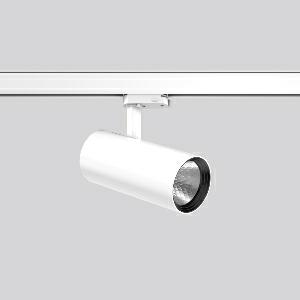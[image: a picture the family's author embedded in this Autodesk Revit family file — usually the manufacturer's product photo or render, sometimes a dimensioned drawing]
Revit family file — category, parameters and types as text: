
# Revit family: deecos_s_mini_742205_002_2_76_f33d
name_source: partatom
category: Lighting Fixtures
units: mm (PartAtom-declared; Revit-internal decimal feet)

## family parameters
Cut with Voids When Loaded = No
Host = Face
Light Source = No
Part Type = Normal
Room Calculation Point = No
Round Connector Dimension = Use Diameter
Shared = No

## types (1)
- DEECOS S mini (1 x LED Modul 927, 3500 lm, 2700)
    Apparent Load = 29 VA
    Approval mark = CE
    CIE Flux Codes = 95 99 100 100 100
    Color Rendering = 92
    Color Temperature = 2700
    Default Elevation = 1800 mm
    Description = Series: DEECOS S mini
LED surface-mounted projector in modern design with no visible cooling ribs. Housing: die-cast aluminium, powder-coated. Rotation range: 356°. Swivel range: 90°. Black plastic ring and recessed LED to prevent glare from the side. Optical assembly with reflector made of MIRO-Silver with 98% total light reflection for outstanding efficiency - can be changed without tools. Best colour rendering index Ra>90. With adapter for RZB 3-circuit DALI tracks. Suitable for Track on ceiling, Wall track. High quality converter without flickering and stroboscopic effect. The following accessories can be mounted without use of tools: interchangeable lenses, decorative glasses, honeycomb louvre, clear and frosted diffusers, white interchangeable plastic ring. 
Colour: traffic white, matt (RAL 9016)
Diameter: 87 mm
Height: 214 mm
Lamp: LED
Socket: without socket
Colour temperature: 2700K
Colour rendering index (CRI): 92
System power: 29 W
Rated luminous flux: 3500 lm
Luminous efficiency: 121 lm/W
Control gear: Converter, dimmable, DALI
Protection class: I
Type of protection: IP 20
    Height = 214 mm
    Lamp = 1 x LED Modul 927
    Lamp Light Flux = 3500 lm
    Lamp count = 1
    Length = 87 mm
    Lifetime = 50000 h
    Luminous efficacy = 121 lm/W
    Manufacturer = RZB
    ModVariant = No
    Model = 742205.002.2.76
    Mounting Place = Ceiling
    Mounting Type = Rail mounted
    Number of Poles = 1
    OnlyDefault = Yes
    Power Factor = 1
    Product Name = DEECOS S mini
    Product group = Track mounted projectors
    ProductGroupID = 301
    Protection Class = Protection class I
    Protection Degree = IP 20
    RLX_Detail_Level = 1
    RLX_Emergency_Light_Flux = 0 lm
    RLX_Emergency_Type = 0
    RLX_Emergency_Type_DB = No
    RlxData = <blob elided: 35217 chars, md5=8ce34caf>
    Socket = socket
    Standby Power = 0 W
    System Light Flux = 3500 lm
    System Power = 29 W
    Type Comments = Product without accessories
    Type Image = 741926.002.jpg
    URL = http://relux.com
    VarID = ---
    Voltage = 230 V
    Voltage Range = 220-240 V
    Weight = 0.00 kg
    Width = 0 mm  [stored 0 ft]

note: [stored X ft] marks values corroborated as IEEE doubles in the binary element streams (Revit-internal decimal feet)

## geometry (parser evidence)
native form markers: Blend x4, Sweep x12
no freeform markers — native parametric forms only
